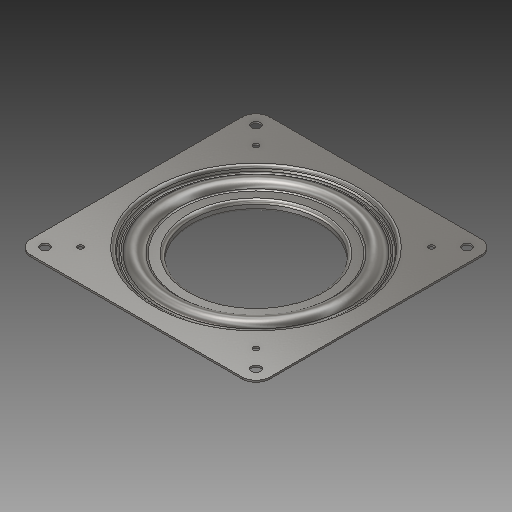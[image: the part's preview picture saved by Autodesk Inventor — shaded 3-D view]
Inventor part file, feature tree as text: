
AUTODESK INVENTOR PART (.ipt)
format: ipt  version: 2018 (Build 220112000, 112)  size: 315,904 bytes
history: native  units: in
note: dims shown in document units (in); Inventor stores cm internally (conversion verified against a paired STEP export)
features: revolve x1
ambient origin geometry x8: Origin, YZ Plane, XZ Plane, XY Plane, X Axis, Y Axis, Z Axis, Center Point
bodies: Solid1 (feature_tree)
feature tree (1):
  revolve  "Revolve2"  [1 undecoded]
note: 1 required parameter value undecoded (feature->parameter linkage not recoverable at this tier; creation-order binding heuristic only, values carry confidence <= 0.55)
